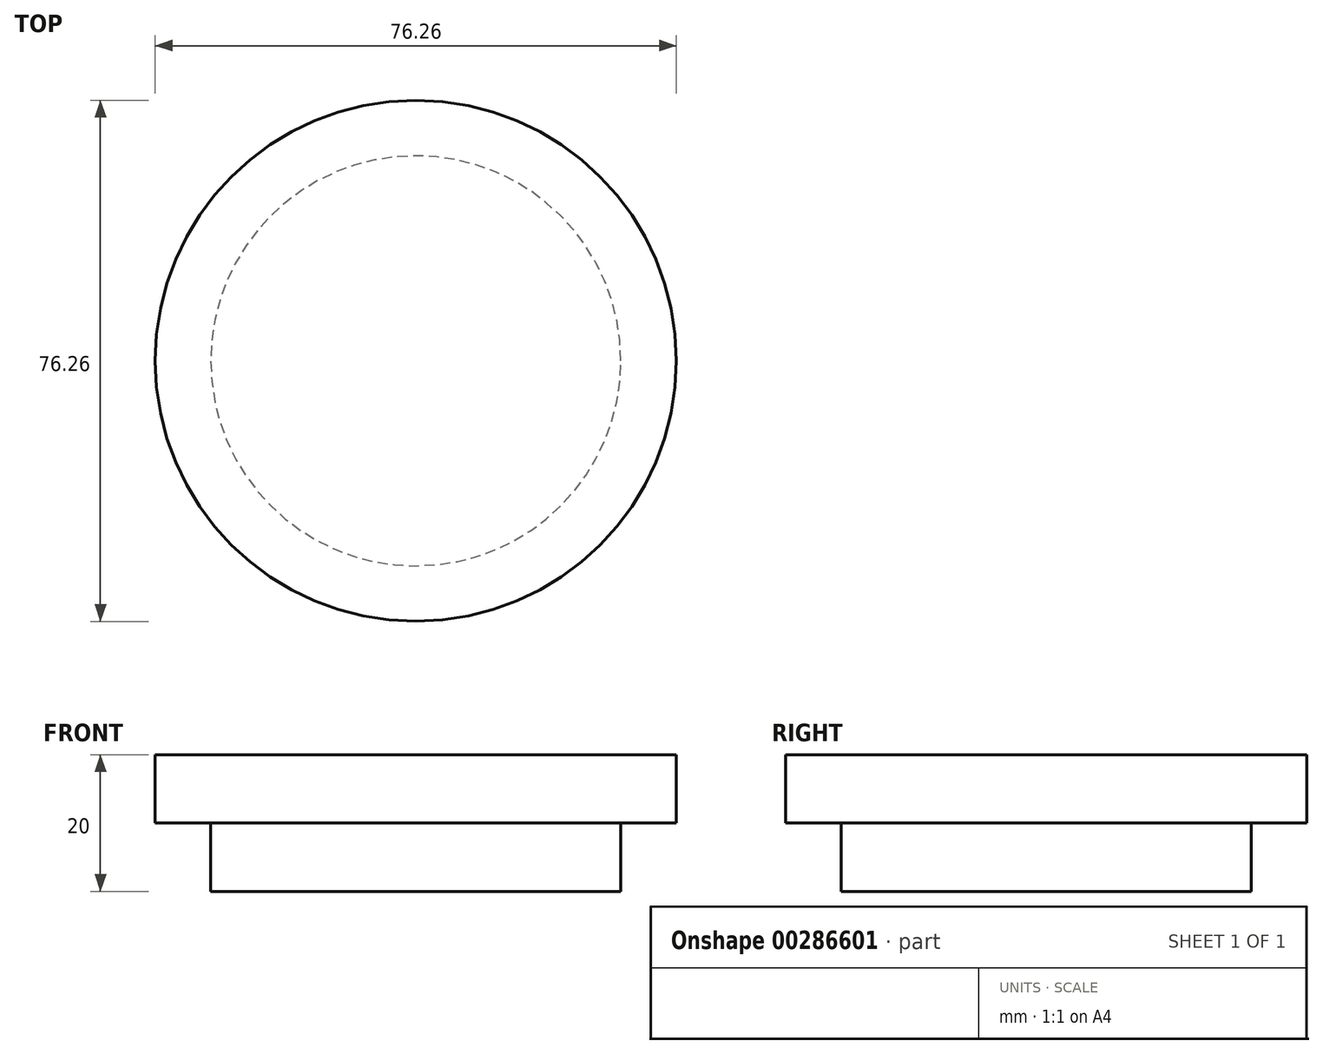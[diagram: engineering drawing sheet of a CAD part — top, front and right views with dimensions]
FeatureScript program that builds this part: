
annotation { "Feature Type Name" : "Feature", "Feature Type Description" : "" }
export const myFeature = defineFeature(function(context is Context, id is Id, definition is map)
    precondition{}
    {
        {
            var Q0;
            Q0=qCreatedBy(makeId("Top.planeOp"),FACE);
            var sketch = newSketch(context, id + "F0", { "sketchPlane" : qUnion([Q0])});
            skCircle(sketch, "E0", {"center": v(0, 0) * mm, "radius": 30 * mm});
            skSolve(sketch);
        }
        {
            var Q0;
            Q0=makeQuery(id+"F0.imprint","IMPRINT",FACE,{"disambiguationData":[TD([[makeQuery(id+"F0.imprint","IMPRINT",EDGE,{"derivedFrom":sQuery(id+"F0.wireOp",EDGE,"E0")}),1.0]])]});
            extrude(context, id + "F1", {"entities" : qUnion([Q0]), "depth" : 10 * mm});
        }
        {
            var Q0;
            Q0=makeQuery(id+"F1.opExtrude","CAP_FACE",FACE,{"disambiguationData":[OSD([sQuery(id+"F0.wireOp",EDGE,"E0")])],"isStart":false});
            var sketch = newSketch(context, id + "F2", { "sketchPlane" : qUnion([Q0])});
            skCircle(sketch, "E1", {"center": v(0, 0) * mm, "radius": 38.13 * mm});
            skSolve(sketch);
        }
        {
            var Q0;
            Q0=makeQuery(id+"F2.imprint","IMPRINT",FACE,{"disambiguationData":[TD([[makeQuery(id+"F2.imprint","IMPRINT",EDGE,{"derivedFrom":makeQuery(id+"F1.opExtrude","CAP_EDGE",EDGE,{"disambiguationData":[OSD([sQuery(id+"F0.wireOp",EDGE,"E0")])],"isStart":false})}),1.0]])]});
            var Q1;
            Q1=makeQuery(id+"F2.imprint","IMPRINT",FACE,{"disambiguationData":[TD([[makeQuery(id+"F2.imprint","IMPRINT",EDGE,{"derivedFrom":sQuery(id+"F2.wireOp",EDGE,"E1")}),1.0]])]});
            extrude(context, id + "F3", {"entities" : qUnion([Q0, Q1]), "operationType" : NewBodyOperationType.ADD, "depth" : 10 * mm});
        }
    });
